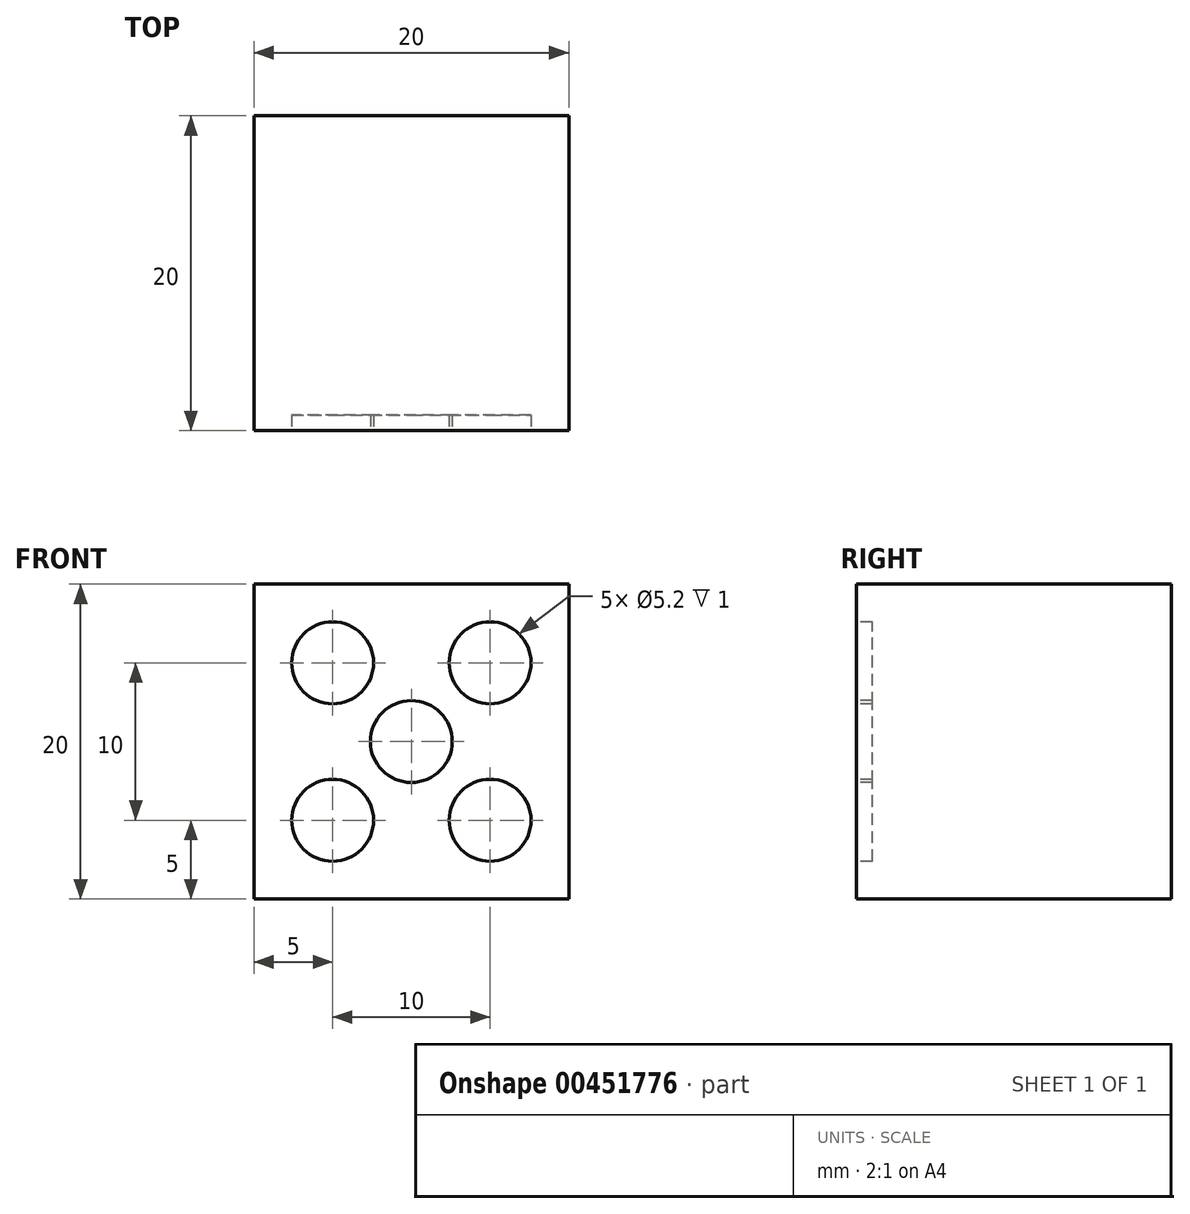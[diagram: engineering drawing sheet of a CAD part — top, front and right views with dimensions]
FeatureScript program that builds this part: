
annotation { "Feature Type Name" : "Feature", "Feature Type Description" : "" }
export const myFeature = defineFeature(function(context is Context, id is Id, definition is map)
    precondition{}
    {
        {
            var Q0;
            Q0=qCreatedBy(makeId("Front.planeOp"),FACE);
            var sketch = newSketch(context, id + "F0", { "sketchPlane" : qUnion([Q0])});
            skLineSegment(sketch, "E0.bottom", {"start": v(0, 0) * mm, "end": v(20, 0) * mm});
            skLineSegment(sketch, "E0.top", {"start": v(0, 20) * mm, "end": v(20, 20) * mm});
            skLineSegment(sketch, "E0.left", {"start": v(0, 0) * mm, "end": v(0, 20) * mm});
            skLineSegment(sketch, "E0.right", {"start": v(20, 0) * mm, "end": v(20, 20) * mm});
            skSolve(sketch);
        }
        {
            var Q0;
            Q0 = qSketchRegion(id + "F0", true);
            extrude(context, id + "F1", {"entities" : qUnion([Q0]), "depth" : 20 * mm});
        }
        {
            var Q0;
            Q0=makeQuery(id+"F1.opExtrude","CAP_FACE",FACE,{"disambiguationData":[OSD([sQuery(id+"F0.wireOp",EDGE,"E0.bottom"),sQuery(id+"F0.wireOp",EDGE,"E0.top"),sQuery(id+"F0.wireOp",EDGE,"E0.left"),sQuery(id+"F0.wireOp",EDGE,"E0.right")])],"isStart":false});
            var sketch = newSketch(context, id + "F2", { "sketchPlane" : qUnion([Q0])});
            skLineSegment(sketch, "E1", {"start": v(10, 20) * mm, "end": v(10, 0) * mm, "construction": true});
            skLineSegment(sketch, "E2", {"start": v(0, 10) * mm, "end": v(20, 10) * mm, "construction": true});
            skLineSegment(sketch, "E3", {"start": v(0, 20) * mm, "end": v(20, 0) * mm, "construction": true});
            skLineSegment(sketch, "E4", {"start": v(0, 0) * mm, "end": v(20, 20) * mm, "construction": true});
            skCircle(sketch, "E5", {"center": v(10, 10) * mm, "radius": 2.6 * mm});
            skCircle(sketch, "E6", {"center": v(5, 15) * mm, "radius": 2.6 * mm});
            skLineSegment(sketch, "E7.MirrorCS", {"start": v(20, 20) * mm, "end": v(0, 0) * mm, "construction": true});
            skCircle(sketch, "E8.MirrorC", {"center": v(15, 5) * mm, "radius": 2.6 * mm});
            skCircle(sketch, "E9.MirrorC", {"center": v(15, 15) * mm, "radius": 2.6 * mm});
            skCircle(sketch, "E10.MirrorC", {"center": v(5, 5) * mm, "radius": 2.6 * mm});
            skSolve(sketch);
        }
        {
            var Q0;
            Q0 = qSketchRegion(id + "F2", true);
            var Q1;
            Q1=makeQuery(id+"F1.opExtrude","CAP_FACE",FACE,{"disambiguationData":[OSD([sQuery(id+"F0.wireOp",EDGE,"E0.bottom"),sQuery(id+"F0.wireOp",EDGE,"E0.top"),sQuery(id+"F0.wireOp",EDGE,"E0.left"),sQuery(id+"F0.wireOp",EDGE,"E0.right")])],"isStart":true});
            extrude(context, id + "F3", {"entities" : qUnion([Q0, Q1]), "operationType" : NewBodyOperationType.REMOVE, "oppositeDirection" : true, "depth" : 1 * mm});
        }
    });
